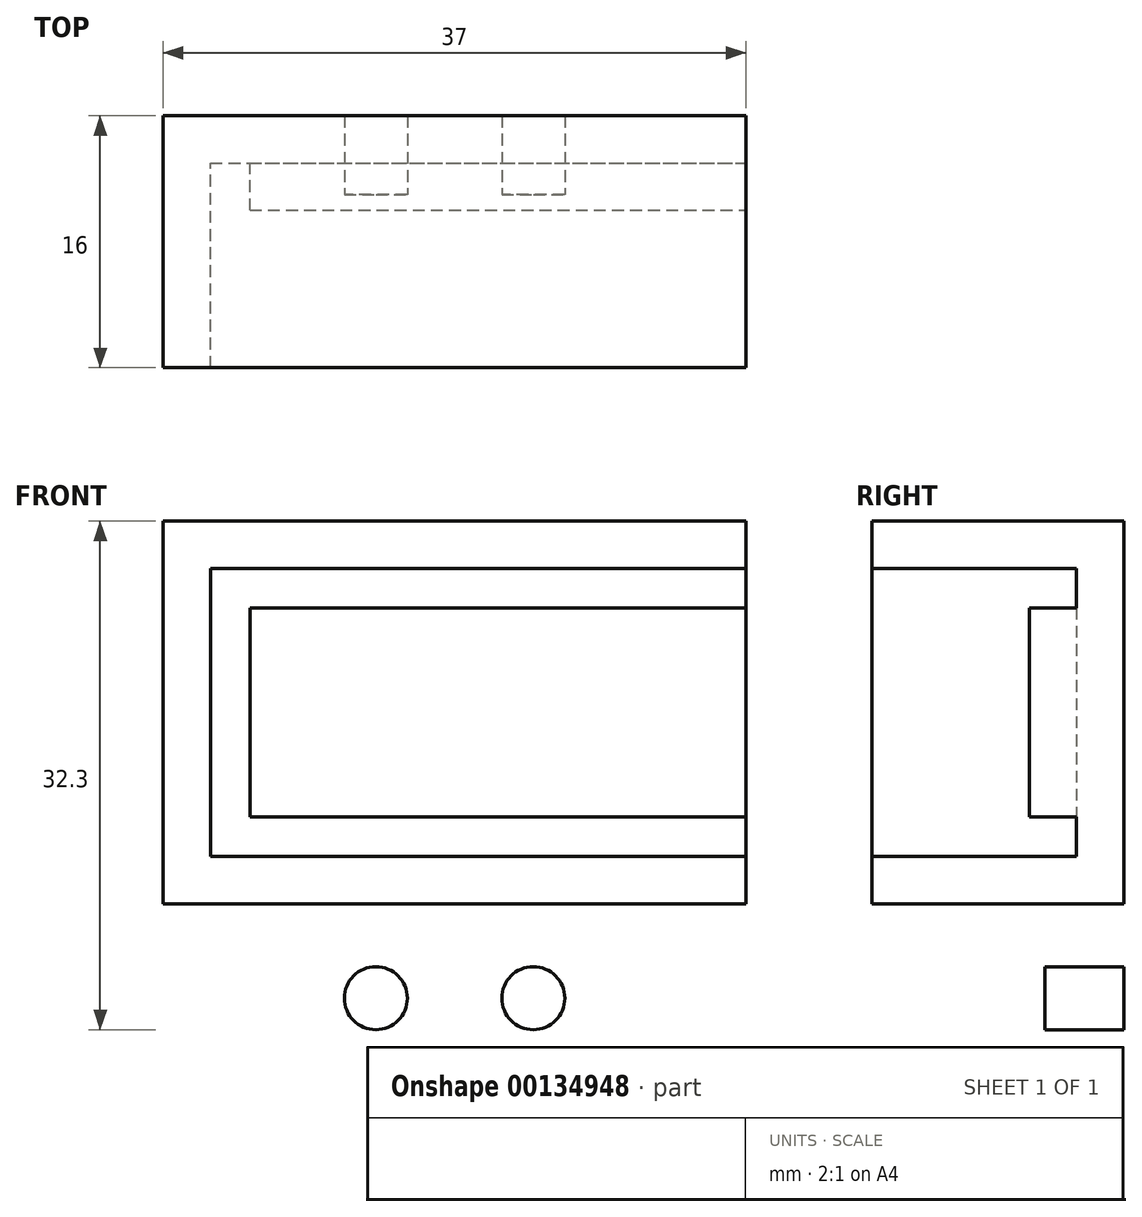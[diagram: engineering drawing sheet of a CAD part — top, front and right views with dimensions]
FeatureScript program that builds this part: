
annotation { "Feature Type Name" : "Feature", "Feature Type Description" : "" }
export const myFeature = defineFeature(function(context is Context, id is Id, definition is map)
    precondition{}
    {
        {
            var Q0;
            Q0=qCreatedBy(makeId("Front.planeOp"),FACE);
            var sketch = newSketch(context, id + "F0", { "sketchPlane" : qUnion([Q0])});
            skLineSegment(sketch, "E0.bottom", {"start": v(0, 0) * mm, "end": v(31, 0) * mm});
            skLineSegment(sketch, "E0.top", {"start": v(0, 18.3) * mm, "end": v(31, 18.3) * mm});
            skLineSegment(sketch, "E0.left", {"start": v(0, 0) * mm, "end": v(0, 18.3) * mm});
            skLineSegment(sketch, "E0.right", {"start": v(31, 0) * mm, "end": v(31, 18.3) * mm});
            skLineSegment(sketch, "E1", {"start": v(0, 9.15) * mm, "end": v(31, 9.15) * mm});
            skLineSegment(sketch, "E2.bottom", {"start": v(34, 21.3) * mm, "end": v(-3, 21.3) * mm});
            skLineSegment(sketch, "E2.top", {"start": v(34, -3) * mm, "end": v(-3, -3) * mm});
            skLineSegment(sketch, "E2.left", {"start": v(34, 21.3) * mm, "end": v(34, -3) * mm});
            skLineSegment(sketch, "E2.right", {"start": v(-3, 21.3) * mm, "end": v(-3, -3) * mm});
            skPoint(sketch, "E2.middle", {"position": v(15.5, 9.15) * mm});
            skSolve(sketch);
        }
        {
            var Q0;
            {var subQ4=sQuery(id+"F0.wireOp",EDGE,"E0.bottom");Q0=makeQuery(id+"F0.imprint","IMPRINT",FACE,{"disambiguationData":[TD([[makeQuery(id+"F0.imprint","IMPRINT",EDGE,{"derivedFrom":subQ4}),-1.0]])]});}
            var Q1;
            {var subQ0=sQuery(id+"F0.wireOp",EDGE,"E0.top");Q1=makeQuery(id+"F0.imprint","IMPRINT",FACE,{"disambiguationData":[TD([[makeQuery(id+"F0.imprint","IMPRINT",EDGE,{"derivedFrom":subQ0}),-1.0]])]});}
            var Q2;
            {var subQ0=sQuery(id+"F0.wireOp",EDGE,"E0.bottom");Q2=makeQuery(id+"F0.imprint","IMPRINT",FACE,{"disambiguationData":[TD([[makeQuery(id+"F0.imprint","IMPRINT",EDGE,{"derivedFrom":subQ0}),1.0]])]});}
            extrude(context, id + "F1", {"entities" : qUnion([Q0, Q1, Q2]), "oppositeDirection" : true, "depth" : 3 * mm});
        }
        {
            var Q0;
            {var subQ4=sQuery(id+"F0.wireOp",EDGE,"E0.bottom");Q0=makeQuery(id+"F0.imprint","IMPRINT",FACE,{"disambiguationData":[TD([[makeQuery(id+"F0.imprint","IMPRINT",EDGE,{"derivedFrom":subQ4}),-1.0]])]});}
            extrude(context, id + "F2", {"entities" : qUnion([Q0]), "operationType" : NewBodyOperationType.ADD, "depth" : 13 * mm});
        }
        {
            var Q0;
            Q0=makeQuery(id+"F2.opExtrude","CAP_FACE",FACE,{"disambiguationData":[OSD([sQuery(id+"F0.wireOp",EDGE,"E0.bottom"),sQuery(id+"F0.wireOp",EDGE,"E0.top"),sQuery(id+"F0.wireOp",EDGE,"E0.left"),sQuery(id+"F0.wireOp",EDGE,"E0.right"),sQuery(id+"F0.wireOp",EDGE,"E2.bottom"),sQuery(id+"F0.wireOp",EDGE,"E2.top"),sQuery(id+"F0.wireOp",EDGE,"E2.left"),sQuery(id+"F0.wireOp",EDGE,"E2.right")])],"isStart":false});
            var sketch = newSketch(context, id + "F3", { "sketchPlane" : qUnion([Q0])});
            skLineSegment(sketch, "E3", {"start": v(31, 18.3) * mm, "end": v(34, 18.3) * mm});
            skLineSegment(sketch, "E4", {"start": v(31, 0) * mm, "end": v(34, 0) * mm});
            skSolve(sketch);
        }
        {
            var Q0;
            {var subQ0=sQuery(id+"F3.wireOp",EDGE,"E3");Q0=makeQuery(id+"F3.imprint","IMPRINT",FACE,{"disambiguationData":[TD([[makeQuery(id+"F3.imprint","IMPRINT",EDGE,{"derivedFrom":subQ0}),-1.0]])]});}
            var Q1;
            Q1=makeQuery(id+"F1.opExtrude","CAP_FACE",FACE,{"disambiguationData":[OSD([sQuery(id+"F0.wireOp",EDGE,"E2.bottom"),sQuery(id+"F0.wireOp",EDGE,"E2.top"),sQuery(id+"F0.wireOp",EDGE,"E2.left"),sQuery(id+"F0.wireOp",EDGE,"E2.right")])],"isStart":true});
            extrude(context, id + "F4", {"entities" : qUnion([Q0]), "operationType" : NewBodyOperationType.REMOVE, "endBound" : BoundingType.UP_TO_SURFACE, "oppositeDirection" : true, "endBoundEntityFace" : qUnion([Q1]), "depth" : 25 * mm});
        }
        {
            var Q0;
            {var subQ0=sQuery(id+"F0.wireOp",EDGE,"E2.right");var subQ1=sQuery(id+"F0.wireOp",EDGE,"E2.left");var subQ2=sQuery(id+"F0.wireOp",EDGE,"E2.top");var subQ3=sQuery(id+"F0.wireOp",EDGE,"E2.bottom");Q0=makeQuery(id+"F4.boolean.opBoolean","MERGE",FACE,{"derivedFrom":[makeQuery(id+"F1.opExtrude","CAP_FACE",FACE,{"disambiguationData":[OSD([subQ3,subQ2,subQ1,subQ0])],"isStart":true}),makeQuery(id+"F4.opExtrude","CAP_FACE",FACE,{"disambiguationData":[OSD([subQ3,subQ2,subQ1,subQ0])],"isStart":false})]});}
            var sketch = newSketch(context, id + "F5", { "sketchPlane" : qUnion([Q0])});
            skLineSegment(sketch, "E5.bottom", {"start": v(2.5, 15.8) * mm, "end": v(31, 15.8) * mm});
            skLineSegment(sketch, "E5.top", {"start": v(2.5, 2.5) * mm, "end": v(31, 2.5) * mm});
            skLineSegment(sketch, "E5.left", {"start": v(2.5, 15.8) * mm, "end": v(2.5, 2.5) * mm});
            skLineSegment(sketch, "E5.right", {"start": v(31, 15.8) * mm, "end": v(31, 2.5) * mm});
            skLineSegment(sketch, "E6", {"start": v(31, 15.8) * mm, "end": v(34, 15.8) * mm});
            skLineSegment(sketch, "E7", {"start": v(34, 15.8) * mm, "end": v(34, 2.5) * mm});
            skLineSegment(sketch, "E8", {"start": v(34, 2.5) * mm, "end": v(31, 2.5) * mm});
            skSolve(sketch);
        }
        {
            var Q0;
            Q0=makeQuery(id+"F5.imprint","IMPRINT",FACE,{"disambiguationData":[TD([[makeQuery(id+"F5.imprint","IMPRINT",EDGE,{"derivedFrom":sQuery(id+"F5.wireOp",EDGE,"E5.bottom")}),-1.0]])]});
            var Q1;
            Q1=makeQuery(id+"F5.imprint","IMPRINT",FACE,{"disambiguationData":[TD([[makeQuery(id+"F5.imprint","IMPRINT",EDGE,{"derivedFrom":sQuery(id+"F5.wireOp",EDGE,"E5.right")}),1.0]])]});
            extrude(context, id + "F6", {"entities" : qUnion([Q0, Q1]), "operationType" : NewBodyOperationType.ADD, "depth" : 3 * mm});
        }
        {
            var Q0;
            {var subQ0=sQuery(id+"F0.wireOp",EDGE,"E2.top");Q0=makeQuery(id+"F2.boolean.opBoolean","MERGE",FACE,{"derivedFrom":[makeQuery(id+"F1.opExtrude","SWEPT_FACE",FACE,{"disambiguationData":[OSD([subQ0])]}),makeQuery(id+"F2.opExtrude","SWEPT_FACE",FACE,{"disambiguationData":[OSD([subQ0])]})]});}
            var sketch = newSketch(context, id + "F7", { "sketchPlane" : qUnion([Q0])});
            skLineSegment(sketch, "E9.bottom", {"start": v(4.5, -3) * mm, "end": v(26.5, -3) * mm});
            skLineSegment(sketch, "E9.top", {"start": v(4.5, 2) * mm, "end": v(26.5, 2) * mm});
            skLineSegment(sketch, "E9.left", {"start": v(4.5, -3) * mm, "end": v(4.5, 2) * mm});
            skLineSegment(sketch, "E9.right", {"start": v(26.5, -3) * mm, "end": v(26.5, 2) * mm});
            skLineSegment(sketch, "E10", {"start": v(4.5, 2) * mm, "end": v(-3, 2) * mm});
            skLineSegment(sketch, "E11", {"start": v(26.5, 2) * mm, "end": v(34, 2) * mm});
            skSolve(sketch);
        }
        {
            var Q0;
            Q0=makeQuery(id+"F7.imprint","IMPRINT",FACE,{"disambiguationData":[TD([[makeQuery(id+"F7.imprint","IMPRINT",EDGE,{"derivedFrom":sQuery(id+"F7.wireOp",EDGE,"E9.bottom")}),-1.0]])]});
            extrude(context, id + "F8", {"entities" : qUnion([Q0]), "operationType" : NewBodyOperationType.ADD, "depth" : 12 * mm});
        }
        {
            var Q0;
            Q0=makeQuery(id+"F8.opExtrude","SWEPT_FACE",FACE,{"disambiguationData":[OSD([sQuery(id+"F7.wireOp",EDGE,"E9.top")])]});
            var sketch = newSketch(context, id + "F9", { "sketchPlane" : qUnion([Q0])});
            skLineSegment(sketch, "E12", {"start": v(4.5, -9) * mm, "end": v(26.5, -9) * mm});
            skCircle(sketch, "E13", {"center": v(10.5, -9) * mm, "radius": 2 * mm});
            skCircle(sketch, "E14", {"center": v(20.5, -9) * mm, "radius": 2 * mm});
            skSolve(sketch);
        }
        {
            var Q0;
            Q0=makeQuery(id+"F8.opExtrude","CAP_EDGE",EDGE,{"disambiguationData":[OSD([sQuery(id+"F7.wireOp",EDGE,"E9.left")])],"isStart":false});
            var Q1;
            Q1=makeQuery(id+"F8.opExtrude","CAP_EDGE",EDGE,{"disambiguationData":[OSD([sQuery(id+"F7.wireOp",EDGE,"E9.left")])],"isStart":true});
            var Q2;
            Q2=makeQuery(id+"F8.opExtrude","CAP_EDGE",EDGE,{"disambiguationData":[OSD([sQuery(id+"F7.wireOp",EDGE,"E9.right")])],"isStart":false});
            var Q3;
            Q3=makeQuery(id+"F8.opExtrude","CAP_EDGE",EDGE,{"disambiguationData":[OSD([sQuery(id+"F7.wireOp",EDGE,"E9.right")])],"isStart":true});
            fillet(context, id + "F10", {"entities" : qUnion([Q0, Q1, Q2, Q3]), "radius" : 5 * mm, "tangentPropagation" : true, "allowEdgeOverflow" : false});
        }
        {
            var Q0;
            {var subQ0=sQuery(id+"F9.wireOp",EDGE,"E13");var subQ1=sQuery(id+"F9.wireOp",EDGE,"E12");var subQ2=makeQuery(id+"F9.imprint","INTERSECT",VERTEX,{"disambiguationData":[OD(0.0)],"derivedFrom":[subQ1,subQ0]});Q0=makeQuery(id+"F9.imprint","IMPRINT",FACE,{"disambiguationData":[TD([[makeQuery(id+"F9.imprint","IMPRINT",EDGE,{"disambiguationData":[TD([[subQ2,-1.0]])],"derivedFrom":subQ1}),1.0]])]});}
            var Q1;
            {var subQ0=sQuery(id+"F9.wireOp",EDGE,"E13");var subQ1=sQuery(id+"F9.wireOp",EDGE,"E12");var subQ2=makeQuery(id+"F9.imprint","INTERSECT",VERTEX,{"disambiguationData":[OD(0.0)],"derivedFrom":[subQ1,subQ0]});Q1=makeQuery(id+"F9.imprint","IMPRINT",FACE,{"disambiguationData":[TD([[makeQuery(id+"F9.imprint","IMPRINT",EDGE,{"disambiguationData":[TD([[subQ2,-1.0]])],"derivedFrom":subQ1}),-1.0]])]});}
            var Q2;
            {var subQ0=sQuery(id+"F9.wireOp",EDGE,"E14");var subQ1=sQuery(id+"F9.wireOp",EDGE,"E12");var subQ2=makeQuery(id+"F9.imprint","INTERSECT",VERTEX,{"disambiguationData":[OD(0.0)],"derivedFrom":[subQ1,subQ0]});Q2=makeQuery(id+"F9.imprint","IMPRINT",FACE,{"disambiguationData":[TD([[makeQuery(id+"F9.imprint","IMPRINT",EDGE,{"disambiguationData":[TD([[subQ2,-1.0]])],"derivedFrom":subQ1}),1.0]])]});}
            var Q3;
            {var subQ0=sQuery(id+"F9.wireOp",EDGE,"E14");var subQ1=sQuery(id+"F9.wireOp",EDGE,"E12");var subQ2=makeQuery(id+"F9.imprint","INTERSECT",VERTEX,{"disambiguationData":[OD(0.0)],"derivedFrom":[subQ1,subQ0]});Q3=makeQuery(id+"F9.imprint","IMPRINT",FACE,{"disambiguationData":[TD([[makeQuery(id+"F9.imprint","IMPRINT",EDGE,{"disambiguationData":[TD([[subQ2,-1.0]])],"derivedFrom":subQ1}),-1.0]])]});}
            extrude(context, id + "F11", {"entities" : qUnion([Q0, Q1, Q2, Q3]), "operationType" : NewBodyOperationType.REMOVE, "oppositeDirection" : true, "depth" : 25 * mm});
        }
    });
